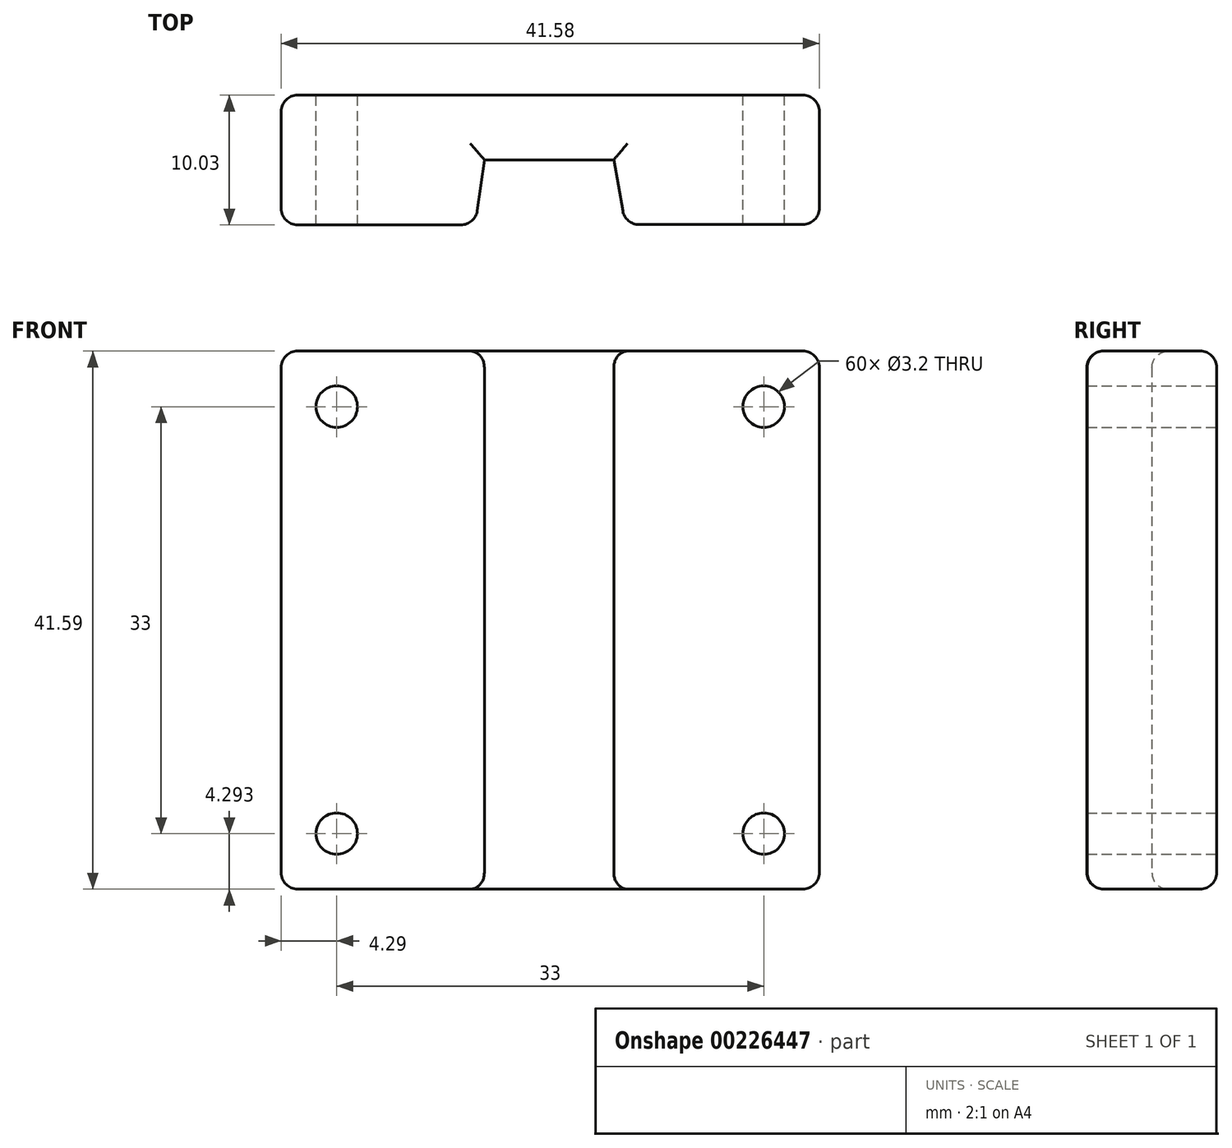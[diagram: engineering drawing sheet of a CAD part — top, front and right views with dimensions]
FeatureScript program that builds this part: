
annotation { "Feature Type Name" : "Feature", "Feature Type Description" : "" }
export const myFeature = defineFeature(function(context is Context, id is Id, definition is map)
    precondition{}
    {
        {
            var Q0;
            Q0=qCreatedBy(makeId("Top.planeOp"),FACE);
            var sketch = newSketch(context, id + "F0", { "sketchPlane" : qUnion([Q0])});
            skLineSegment(sketch, "E0", {"start": v(-20.8, -5.03) * mm, "end": v(-5.8, -5.03) * mm});
            skLineSegment(sketch, "E1", {"start": v(-5.8, -5.03) * mm, "end": v(-5.09, 0) * mm});
            skLineSegment(sketch, "E2", {"start": v(-5.09, 0) * mm, "end": v(4.91, 0) * mm});
            skLineSegment(sketch, "E3", {"start": v(4.91, 0) * mm, "end": v(5.8, -5) * mm});
            skLineSegment(sketch, "E4", {"start": v(5.8, -5) * mm, "end": v(20.8, -5) * mm});
            skLineSegment(sketch, "E5", {"start": v(20.8, -5) * mm, "end": v(20.8, -1.35) * mm});
            skLineSegment(sketch, "E6", {"start": v(19.64, 5) * mm, "end": v(-14.44, 5) * mm});
            skLineSegment(sketch, "E7", {"start": v(-20.8, -1.35) * mm, "end": v(-20.8, -5.03) * mm});
            skLineSegment(sketch, "E8", {"start": v(20.8, -5) * mm, "end": v(-20.8, 5) * mm, "construction": true});
            skPoint(sketch, "E9", {"position": v(0, 0) * mm});
            skPoint(sketch, "E10.visualSharp", {"position": v(-20.8, 5) * mm});
            skPoint(sketch, "E11.visualSharp", {"position": v(20.8, 5) * mm});
            skLineSegment(sketch, "E12", {"start": v(20.8, -1.35) * mm, "end": v(20.8, 5) * mm});
            skLineSegment(sketch, "E13", {"start": v(19.64, 5) * mm, "end": v(20.8, 5) * mm});
            skLineSegment(sketch, "E14", {"start": v(-14.44, 5) * mm, "end": v(-20.8, 5) * mm});
            skLineSegment(sketch, "E15", {"start": v(-20.8, 5) * mm, "end": v(-20.8, -1.35) * mm});
            skSolve(sketch);
        }
        {
            var Q0;
            Q0=makeQuery(id+"F0.imprint","IMPRINT",FACE,{"disambiguationData":[TD([[makeQuery(id+"F0.imprint","IMPRINT",EDGE,{"derivedFrom":sQuery(id+"F0.wireOp",EDGE,"E0")}),1.0]])]});
            extrude(context, id + "F1", {"entities" : qUnion([Q0]), "depth" : 41.6 * mm, "offsetDistance" : 25.4 * mm});
        }
        {
            var Q0;
            Q0=makeQuery(id+"F1.opExtrude","SWEPT_FACE",FACE,{"disambiguationData":[OSD([sQuery(id+"F0.wireOp",EDGE,"E6")])]});
            var sketch = newSketch(context, id + "F2", { "sketchPlane" : qUnion([Q0])});
            skCircle(sketch, "E16", {"center": v(-16.5, 37.3) * mm, "radius": 1.6 * mm});
            skCircle(sketch, "E17", {"center": v(16.5, 37.3) * mm, "radius": 1.6 * mm});
            skCircle(sketch, "E18", {"center": v(16.5, 4.3) * mm, "radius": 1.6 * mm});
            skCircle(sketch, "E19", {"center": v(-16.5, 4.3) * mm, "radius": 1.6 * mm});
            skLineSegment(sketch, "E20.bottom", {"start": v(-16.5, 37.3) * mm, "end": v(16.5, 37.3) * mm});
            skLineSegment(sketch, "E20.top", {"start": v(-16.5, 4.3) * mm, "end": v(16.5, 4.3) * mm});
            skLineSegment(sketch, "E20.left", {"start": v(-16.5, 37.3) * mm, "end": v(-16.5, 4.3) * mm});
            skLineSegment(sketch, "E20.right", {"start": v(16.5, 37.3) * mm, "end": v(16.5, 4.3) * mm});
            skLineSegment(sketch, "E21", {"start": v(0, 41.59) * mm, "end": v(0, 0) * mm});
            skLineSegment(sketch, "E22", {"start": v(20.8, 20.8) * mm, "end": v(-20.8, 20.8) * mm});
            skPoint(sketch, "E23", {"position": v(0, 20.8) * mm});
            skLineSegment(sketch, "E24", {"start": v(20.8, 41.59) * mm, "end": v(-20.8, 0) * mm});
            skLineSegment(sketch, "E25", {"start": v(-20.8, 41.59) * mm, "end": v(20.8, 0) * mm});
            skSolve(sketch);
        }
        {
            var Q0;
            {var subQ0=sQuery(id+"F2.wireOp",EDGE,"GrC9rXH3-9UHd-gBO8-3bFG-osErbcmIHNc7");var subQ1=makeQuery(id+"F2.imprint","INTERSECT",VERTEX,{"derivedFrom":[subQ0,sQuery(id+"F2.wireOp",EDGE,"8eb7g6iP-JeB2-ZfLy-NJdU-ASClG6dUrgVS")]});Q0=makeQuery(id+"F2.imprint","IMPRINT",FACE,{"disambiguationData":[TD([[makeQuery(id+"F2.imprint","IMPRINT",EDGE,{"disambiguationData":[TD([[subQ1,1.0]])],"derivedFrom":subQ0}),-1.0]])]});}
            var Q1;
            {var subQ0=sQuery(id+"F2.wireOp",EDGE,"8eb7g6iP-JeB2-ZfLy-NJdU-ASClG6dUrgVS");var subQ1=sQuery(id+"F2.wireOp",EDGE,"GrC9rXH3-9UHd-gBO8-3bFG-osErbcmIHNc7");var subQ2=makeQuery(id+"F2.imprint","INTERSECT",VERTEX,{"derivedFrom":[subQ1,subQ0]});Q1=makeQuery(id+"F2.imprint","IMPRINT",FACE,{"disambiguationData":[TD([[makeQuery(id+"F2.imprint","IMPRINT",EDGE,{"disambiguationData":[TD([[subQ2,-1.0]])],"derivedFrom":subQ1}),1.0]])]});}
            var Q2;
            {var subQ0=sQuery(id+"F2.wireOp",EDGE,"8eb7g6iP-JeB2-ZfLy-NJdU-ASClG6dUrgVS");var subQ1=sQuery(id+"F2.wireOp",EDGE,"GrC9rXH3-9UHd-gBO8-3bFG-osErbcmIHNc7");var subQ2=makeQuery(id+"F2.imprint","INTERSECT",VERTEX,{"derivedFrom":[subQ1,subQ0]});Q2=makeQuery(id+"F2.imprint","IMPRINT",FACE,{"disambiguationData":[TD([[makeQuery(id+"F2.imprint","IMPRINT",EDGE,{"disambiguationData":[TD([[subQ2,1.0]])],"derivedFrom":subQ1}),1.0]])]});}
            var Q3;
            {var subQ0=sQuery(id+"F2.wireOp",EDGE,"lZcTnU50-SuSA-eqHt-mNmg-zvj1KI8RxS0C");var subQ1=sQuery(id+"F2.wireOp",EDGE,"GrC9rXH3-9UHd-gBO8-3bFG-osErbcmIHNc7");var subQ2=makeQuery(id+"F2.imprint","INTERSECT",VERTEX,{"derivedFrom":[subQ1,subQ0]});Q3=makeQuery(id+"F2.imprint","IMPRINT",FACE,{"disambiguationData":[TD([[makeQuery(id+"F2.imprint","IMPRINT",EDGE,{"disambiguationData":[TD([[subQ2,1.0]])],"derivedFrom":subQ1}),-1.0]])]});}
            var Q4;
            {var subQ0=sQuery(id+"F2.wireOp",EDGE,"lZcTnU50-SuSA-eqHt-mNmg-zvj1KI8RxS0C");var subQ1=sQuery(id+"F2.wireOp",EDGE,"GrC9rXH3-9UHd-gBO8-3bFG-osErbcmIHNc7");var subQ2=makeQuery(id+"F2.imprint","INTERSECT",VERTEX,{"derivedFrom":[subQ1,subQ0]});Q4=makeQuery(id+"F2.imprint","IMPRINT",FACE,{"disambiguationData":[TD([[makeQuery(id+"F2.imprint","IMPRINT",EDGE,{"disambiguationData":[TD([[subQ2,-1.0]])],"derivedFrom":subQ1}),-1.0]])]});}
            var Q5;
            {var subQ0=sQuery(id+"F2.wireOp",EDGE,"GrC9rXH3-9UHd-gBO8-3bFG-osErbcmIHNc7");var subQ1=makeQuery(id+"F2.imprint","INTERSECT",VERTEX,{"derivedFrom":[subQ0,sQuery(id+"F2.wireOp",EDGE,"lZcTnU50-SuSA-eqHt-mNmg-zvj1KI8RxS0C")]});Q5=makeQuery(id+"F2.imprint","IMPRINT",FACE,{"disambiguationData":[TD([[makeQuery(id+"F2.imprint","IMPRINT",EDGE,{"disambiguationData":[TD([[subQ1,1.0]])],"derivedFrom":subQ0}),1.0]])]});}
            var Q6;
            {var subQ0=sQuery(id+"F2.wireOp",EDGE,"E20.bottom");var subQ1=sQuery(id+"F2.wireOp",EDGE,"E17");var subQ2=makeQuery(id+"F2.imprint","INTERSECT",VERTEX,{"derivedFrom":[subQ1,subQ0]});Q6=makeQuery(id+"F2.imprint","IMPRINT",FACE,{"disambiguationData":[TD([[makeQuery(id+"F2.imprint","IMPRINT",EDGE,{"disambiguationData":[TD([[subQ2,-1.0]])],"derivedFrom":subQ1}),1.0]])]});}
            var Q7;
            {var subQ0=sQuery(id+"F2.wireOp",EDGE,"UkBU6BXG-6uwA-i5xQ-b2Hl-T7reDA5RtHgX");var subQ1=sQuery(id+"F2.wireOp",EDGE,"E17");var subQ2=makeQuery(id+"F2.imprint","INTERSECT",VERTEX,{"derivedFrom":[subQ1,subQ0]});Q7=makeQuery(id+"F2.imprint","IMPRINT",FACE,{"disambiguationData":[TD([[makeQuery(id+"F2.imprint","IMPRINT",EDGE,{"disambiguationData":[TD([[subQ2,-1.0]])],"derivedFrom":subQ1}),1.0]])]});}
            var Q8;
            {var subQ1=sQuery(id+"F2.wireOp",EDGE,"uMzIfTd4-Jex7-TaPJ-SM1q-krGrRvYBssnI");var subQ3=sQuery(id+"F2.wireOp",EDGE,"E17");var subQ4=makeQuery(id+"F2.imprint","INTERSECT",VERTEX,{"derivedFrom":[subQ1,subQ3]});Q8=makeQuery(id+"F2.imprint","IMPRINT",FACE,{"disambiguationData":[TD([[makeQuery(id+"F2.imprint","IMPRINT",EDGE,{"disambiguationData":[TD([[subQ4,1.0]])],"derivedFrom":subQ3}),1.0]])]});}
            var Q9;
            {var subQ1=sQuery(id+"F2.wireOp",EDGE,"uMzIfTd4-Jex7-TaPJ-SM1q-krGrRvYBssnI");var subQ3=sQuery(id+"F2.wireOp",EDGE,"E17");var subQ4=makeQuery(id+"F2.imprint","INTERSECT",VERTEX,{"derivedFrom":[subQ1,subQ3]});Q9=makeQuery(id+"F2.imprint","IMPRINT",FACE,{"disambiguationData":[TD([[makeQuery(id+"F2.imprint","IMPRINT",EDGE,{"disambiguationData":[TD([[subQ4,-1.0]])],"derivedFrom":subQ3}),1.0]])]});}
            var Q10;
            {var subQ0=sQuery(id+"F2.wireOp",EDGE,"E20.left");var subQ1=sQuery(id+"F2.wireOp",EDGE,"E16");var subQ2=makeQuery(id+"F2.imprint","INTERSECT",VERTEX,{"derivedFrom":[subQ1,subQ0]});Q10=makeQuery(id+"F2.imprint","IMPRINT",FACE,{"disambiguationData":[TD([[makeQuery(id+"F2.imprint","IMPRINT",EDGE,{"disambiguationData":[TD([[subQ2,-1.0]])],"derivedFrom":subQ1}),1.0]])]});}
            var Q11;
            {var subQ0=sQuery(id+"F2.wireOp",EDGE,"E20.bottom");var subQ1=sQuery(id+"F2.wireOp",EDGE,"E16");var subQ2=makeQuery(id+"F2.imprint","INTERSECT",VERTEX,{"derivedFrom":[subQ1,subQ0]});Q11=makeQuery(id+"F2.imprint","IMPRINT",FACE,{"disambiguationData":[TD([[makeQuery(id+"F2.imprint","IMPRINT",EDGE,{"disambiguationData":[TD([[subQ2,1.0]])],"derivedFrom":subQ1}),1.0]])]});}
            var Q12;
            {var subQ1=sQuery(id+"F2.wireOp",EDGE,"KNTZyyw6-Hckl-Q271-iIQe-2PqkrOmCT1su");var subQ3=sQuery(id+"F2.wireOp",EDGE,"E16");var subQ4=makeQuery(id+"F2.imprint","INTERSECT",VERTEX,{"derivedFrom":[subQ1,subQ3]});Q12=makeQuery(id+"F2.imprint","IMPRINT",FACE,{"disambiguationData":[TD([[makeQuery(id+"F2.imprint","IMPRINT",EDGE,{"disambiguationData":[TD([[subQ4,1.0]])],"derivedFrom":subQ3}),1.0]])]});}
            var Q13;
            {var subQ1=sQuery(id+"F2.wireOp",EDGE,"KNTZyyw6-Hckl-Q271-iIQe-2PqkrOmCT1su");var subQ3=sQuery(id+"F2.wireOp",EDGE,"E16");var subQ4=makeQuery(id+"F2.imprint","INTERSECT",VERTEX,{"derivedFrom":[subQ1,subQ3]});Q13=makeQuery(id+"F2.imprint","IMPRINT",FACE,{"disambiguationData":[TD([[makeQuery(id+"F2.imprint","IMPRINT",EDGE,{"disambiguationData":[TD([[subQ4,-1.0]])],"derivedFrom":subQ3}),1.0]])]});}
            var Q14;
            {var subQ0=sQuery(id+"F2.wireOp",EDGE,"5JB2wuRv-3SnY-JfgK-DCdv-r9ns0gsCGs5U");var subQ1=sQuery(id+"F2.wireOp",EDGE,"E19");var subQ2=makeQuery(id+"F2.imprint","INTERSECT",VERTEX,{"derivedFrom":[subQ1,subQ0]});Q14=makeQuery(id+"F2.imprint","IMPRINT",FACE,{"disambiguationData":[TD([[makeQuery(id+"F2.imprint","IMPRINT",EDGE,{"disambiguationData":[TD([[subQ2,-1.0]])],"derivedFrom":subQ1}),1.0]])]});}
            var Q15;
            {var subQ0=sQuery(id+"F2.wireOp",EDGE,"5JB2wuRv-3SnY-JfgK-DCdv-r9ns0gsCGs5U");var subQ1=sQuery(id+"F2.wireOp",EDGE,"E19");var subQ2=makeQuery(id+"F2.imprint","INTERSECT",VERTEX,{"derivedFrom":[subQ1,subQ0]});Q15=makeQuery(id+"F2.imprint","IMPRINT",FACE,{"disambiguationData":[TD([[makeQuery(id+"F2.imprint","IMPRINT",EDGE,{"disambiguationData":[TD([[subQ2,1.0]])],"derivedFrom":subQ1}),1.0]])]});}
            var Q16;
            {var subQ1=sQuery(id+"F2.wireOp",EDGE,"x9yeLiOu-jXsP-ngz8-OfoG-MhONXggG2Zbb");var subQ3=sQuery(id+"F2.wireOp",EDGE,"E19");var subQ4=makeQuery(id+"F2.imprint","INTERSECT",VERTEX,{"derivedFrom":[subQ1,subQ3]});Q16=makeQuery(id+"F2.imprint","IMPRINT",FACE,{"disambiguationData":[TD([[makeQuery(id+"F2.imprint","IMPRINT",EDGE,{"disambiguationData":[TD([[subQ4,-1.0]])],"derivedFrom":subQ3}),1.0]])]});}
            var Q17;
            {var subQ1=sQuery(id+"F2.wireOp",EDGE,"x9yeLiOu-jXsP-ngz8-OfoG-MhONXggG2Zbb");var subQ3=sQuery(id+"F2.wireOp",EDGE,"E19");var subQ4=makeQuery(id+"F2.imprint","INTERSECT",VERTEX,{"derivedFrom":[subQ1,subQ3]});Q17=makeQuery(id+"F2.imprint","IMPRINT",FACE,{"disambiguationData":[TD([[makeQuery(id+"F2.imprint","IMPRINT",EDGE,{"disambiguationData":[TD([[subQ4,1.0]])],"derivedFrom":subQ3}),1.0]])]});}
            var Q18;
            {var subQ1=sQuery(id+"F2.wireOp",EDGE,"zqcfac3f-cAye-eitb-DHrz-wdVLipgtgNFC");var subQ3=sQuery(id+"F2.wireOp",EDGE,"E18");var subQ4=makeQuery(id+"F2.imprint","INTERSECT",VERTEX,{"derivedFrom":[subQ1,subQ3]});Q18=makeQuery(id+"F2.imprint","IMPRINT",FACE,{"disambiguationData":[TD([[makeQuery(id+"F2.imprint","IMPRINT",EDGE,{"disambiguationData":[TD([[subQ4,1.0]])],"derivedFrom":subQ3}),1.0]])]});}
            var Q19;
            {var subQ1=sQuery(id+"F2.wireOp",EDGE,"zqcfac3f-cAye-eitb-DHrz-wdVLipgtgNFC");var subQ3=sQuery(id+"F2.wireOp",EDGE,"E18");var subQ4=makeQuery(id+"F2.imprint","INTERSECT",VERTEX,{"derivedFrom":[subQ1,subQ3]});Q19=makeQuery(id+"F2.imprint","IMPRINT",FACE,{"disambiguationData":[TD([[makeQuery(id+"F2.imprint","IMPRINT",EDGE,{"disambiguationData":[TD([[subQ4,-1.0]])],"derivedFrom":subQ3}),1.0]])]});}
            var Q20;
            {var subQ0=sQuery(id+"F2.wireOp",EDGE,"9J1KCppP-FWMB-5r08-hWcM-QjkxT2uAeGby");var subQ1=sQuery(id+"F2.wireOp",EDGE,"E18");var subQ2=makeQuery(id+"F2.imprint","INTERSECT",VERTEX,{"derivedFrom":[subQ1,subQ0]});Q20=makeQuery(id+"F2.imprint","IMPRINT",FACE,{"disambiguationData":[TD([[makeQuery(id+"F2.imprint","IMPRINT",EDGE,{"disambiguationData":[TD([[subQ2,1.0]])],"derivedFrom":subQ1}),1.0]])]});}
            var Q21;
            {var subQ0=sQuery(id+"F2.wireOp",EDGE,"9J1KCppP-FWMB-5r08-hWcM-QjkxT2uAeGby");var subQ1=sQuery(id+"F2.wireOp",EDGE,"E18");var subQ2=makeQuery(id+"F2.imprint","INTERSECT",VERTEX,{"derivedFrom":[subQ1,subQ0]});Q21=makeQuery(id+"F2.imprint","IMPRINT",FACE,{"disambiguationData":[TD([[makeQuery(id+"F2.imprint","IMPRINT",EDGE,{"disambiguationData":[TD([[subQ2,-1.0]])],"derivedFrom":subQ1}),1.0]])]});}
            extrude(context, id + "F3", {"entities" : qUnion([Q0, Q1, Q2, Q3, Q4, Q5, Q6, Q7, Q8, Q9, Q10, Q11, Q12, Q13, Q14, Q15, Q16, Q17, Q18, Q19, Q20, Q21]), "operationType" : NewBodyOperationType.REMOVE, "oppositeDirection" : true, "depth" : 25.4 * mm});
        }
        {
            var Q0;
            Q0=makeQuery(id+"F1.opExtrude","CAP_EDGE",EDGE,{"disambiguationData":[OSD([sQuery(id+"F0.wireOp",EDGE,"E6")])],"isStart":false});
            var Q1;
            Q1=makeQuery(id+"F1.opExtrude","CAP_EDGE",EDGE,{"disambiguationData":[OSD([sQuery(id+"F0.wireOp",EDGE,"E6")])],"isStart":true});
            var Q2;
            Q2=makeQuery(id+"F1.opExtrude","CAP_EDGE",EDGE,{"disambiguationData":[OSD([sQuery(id+"F0.wireOp",EDGE,"E4")])],"isStart":true});
            var Q3;
            Q3=makeQuery(id+"F1.opExtrude","CAP_EDGE",EDGE,{"disambiguationData":[OSD([sQuery(id+"F0.wireOp",EDGE,"E0")])],"isStart":true});
            var Q4;
            Q4=makeQuery(id+"F1.opExtrude","SWEPT_EDGE",EDGE,{"disambiguationData":[OSD([sQuery(id+"F0.wireOp",EDGE,"E12"),sQuery(id+"F0.wireOp",EDGE,"E13")])]});
            var Q5;
            Q5=makeQuery(id+"F1.opExtrude","SWEPT_EDGE",EDGE,{"disambiguationData":[OSD([sQuery(id+"F0.wireOp",EDGE,"E14"),sQuery(id+"F0.wireOp",EDGE,"E15")])]});
            var Q6;
            Q6=makeQuery(id+"F1.opExtrude","SWEPT_EDGE",EDGE,{"disambiguationData":[OSD([sQuery(id+"F0.wireOp",EDGE,"E4"),sQuery(id+"F0.wireOp",EDGE,"E5")])]});
            var Q7;
            Q7=makeQuery(id+"F1.opExtrude","SWEPT_EDGE",EDGE,{"disambiguationData":[OSD([sQuery(id+"F0.wireOp",EDGE,"E3"),sQuery(id+"F0.wireOp",EDGE,"E4")])]});
            var Q8;
            Q8=makeQuery(id+"F1.opExtrude","SWEPT_EDGE",EDGE,{"disambiguationData":[OSD([sQuery(id+"F0.wireOp",EDGE,"E0"),sQuery(id+"F0.wireOp",EDGE,"E1")])]});
            var Q9;
            Q9=makeQuery(id+"F1.opExtrude","SWEPT_EDGE",EDGE,{"disambiguationData":[OSD([sQuery(id+"F0.wireOp",EDGE,"E0"),sQuery(id+"F0.wireOp",EDGE,"E7")])]});
            var Q10;
            Q10=makeQuery(id+"F1.opExtrude","SWEPT_FACE",FACE,{"disambiguationData":[OSD([sQuery(id+"F0.wireOp",EDGE,"E7"),sQuery(id+"F0.wireOp",EDGE,"E15")])]});
            var Q11;
            Q11=makeQuery(id+"F1.opExtrude","CAP_FACE",FACE,{"disambiguationData":[OSD([sQuery(id+"F0.wireOp",EDGE,"E0"),sQuery(id+"F0.wireOp",EDGE,"E1"),sQuery(id+"F0.wireOp",EDGE,"E2"),sQuery(id+"F0.wireOp",EDGE,"E3"),sQuery(id+"F0.wireOp",EDGE,"E4"),sQuery(id+"F0.wireOp",EDGE,"E5"),sQuery(id+"F0.wireOp",EDGE,"E6"),sQuery(id+"F0.wireOp",EDGE,"E7"),sQuery(id+"F0.wireOp",EDGE,"E12"),sQuery(id+"F0.wireOp",EDGE,"E13"),sQuery(id+"F0.wireOp",EDGE,"E14"),sQuery(id+"F0.wireOp",EDGE,"E15")])],"isStart":false});
            var Q12;
            Q12=makeQuery(id+"F1.opExtrude","CAP_FACE",FACE,{"disambiguationData":[OSD([sQuery(id+"F0.wireOp",EDGE,"E0"),sQuery(id+"F0.wireOp",EDGE,"E1"),sQuery(id+"F0.wireOp",EDGE,"E2"),sQuery(id+"F0.wireOp",EDGE,"E3"),sQuery(id+"F0.wireOp",EDGE,"E4"),sQuery(id+"F0.wireOp",EDGE,"E5"),sQuery(id+"F0.wireOp",EDGE,"E6"),sQuery(id+"F0.wireOp",EDGE,"E7"),sQuery(id+"F0.wireOp",EDGE,"E12"),sQuery(id+"F0.wireOp",EDGE,"E13"),sQuery(id+"F0.wireOp",EDGE,"E14"),sQuery(id+"F0.wireOp",EDGE,"E15")])],"isStart":true});
            fillet(context, id + "F4", {"entities" : qUnion([Q0, Q1, Q2, Q3, Q4, Q5, Q6, Q7, Q8, Q9, Q10, Q11, Q12]), "radius" : 1.27 * mm, "tangentPropagation" : true, "allowEdgeOverflow" : false});
        }
    });
